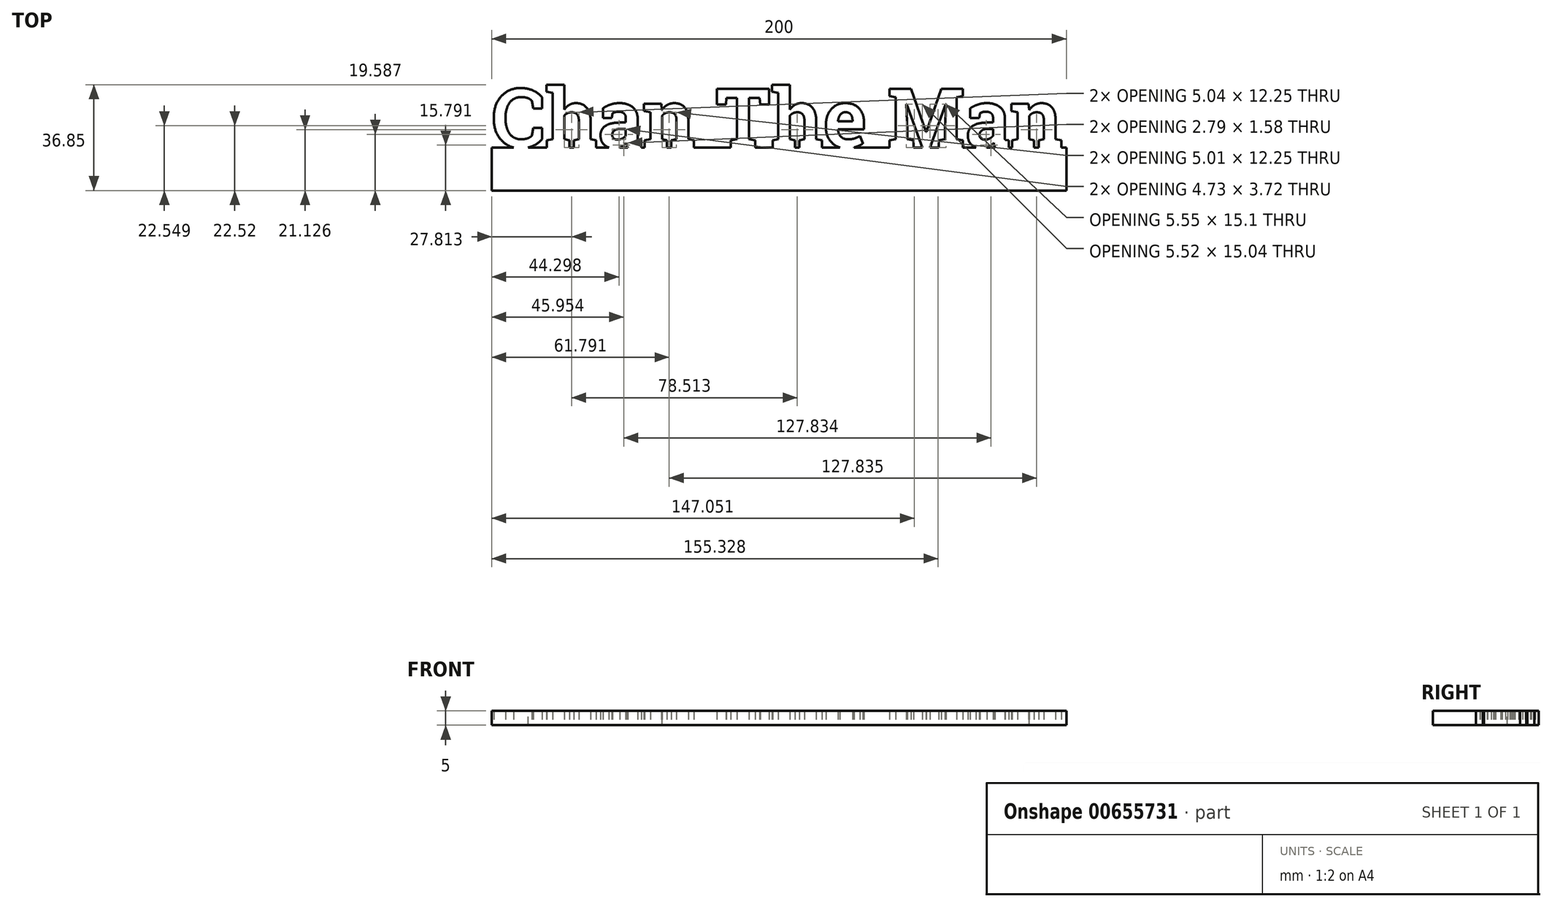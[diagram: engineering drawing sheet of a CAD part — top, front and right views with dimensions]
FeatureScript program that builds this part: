
annotation { "Feature Type Name" : "Feature", "Feature Type Description" : "" }
export const myFeature = defineFeature(function(context is Context, id is Id, definition is map)
    precondition{}
    {
        {
            var Q0;
            Q0=qCreatedBy(makeId("Top.planeOp"),FACE);
            var sketch = newSketch(context, id + "F0", { "sketchPlane" : qUnion([Q0])});
            skText(sketch, "E0", { "text": "Chan The Man", "fontName": "RobotoSlab-Bold.ttf"});
            skLineSegment(sketch, "E1", {"start": v(-100, 0) * mm, "end": v(100, 0) * mm});
            skLineSegment(sketch, "E2", {"start": v(100, 0) * mm, "end": v(100, -15) * mm});
            skLineSegment(sketch, "E3", {"start": v(100, -15) * mm, "end": v(-100, -15) * mm});
            skLineSegment(sketch, "E4", {"start": v(-100, -15) * mm, "end": v(-100, 0) * mm});
            const initialGuessF0  = {"E0": [-0.1, 0, 1, 0, 0.02065]};
            skSetInitialGuess(sketch, initialGuessF0);
            skSolve(sketch);
        }
        {
            var Q0;
            Q0 = qSketchRegion(id + "F0", true);
            extrude(context, id + "F1", {"entities" : qUnion([Q0]), "depth" : 5 * mm, "offsetDistance" : 25 * mm});
        }
    });
